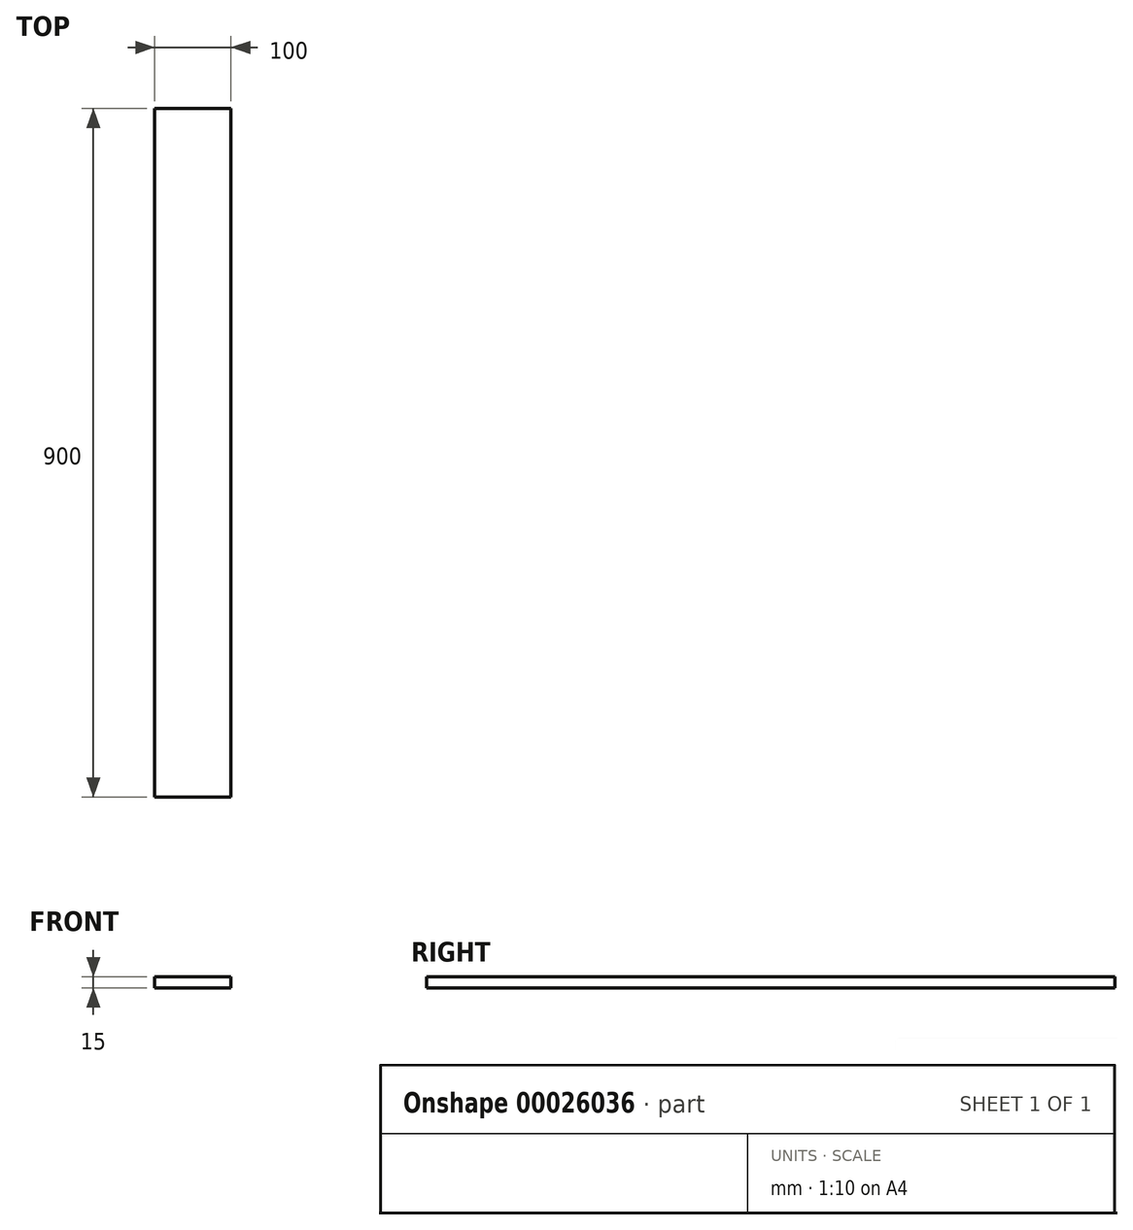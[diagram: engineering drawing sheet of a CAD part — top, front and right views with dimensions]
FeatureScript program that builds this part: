
annotation { "Feature Type Name" : "Feature", "Feature Type Description" : "" }
export const myFeature = defineFeature(function(context is Context, id is Id, definition is map)
    precondition{}
    {
        {
            var Q0;
            Q0=qCreatedBy(makeId("Front.planeOp"),FACE);
            var sketch = newSketch(context, id + "F0", { "sketchPlane" : qUnion([Q0])});
            skLineSegment(sketch, "E0.bottom", {"start": v(0, 0) * mm, "end": v(100, 0) * mm});
            skLineSegment(sketch, "E0.top", {"start": v(0, 15) * mm, "end": v(100, 15) * mm});
            skLineSegment(sketch, "E0.left", {"start": v(0, 0) * mm, "end": v(0, 15) * mm});
            skLineSegment(sketch, "E0.right", {"start": v(100, 0) * mm, "end": v(100, 15) * mm});
            skSolve(sketch);
        }
        {
            var Q0;
            Q0 = qSketchRegion(id + "F0", true);
            extrude(context, id + "F1", {"entities" : qUnion([Q0]), "depth" : 900 * mm});
        }
    });
